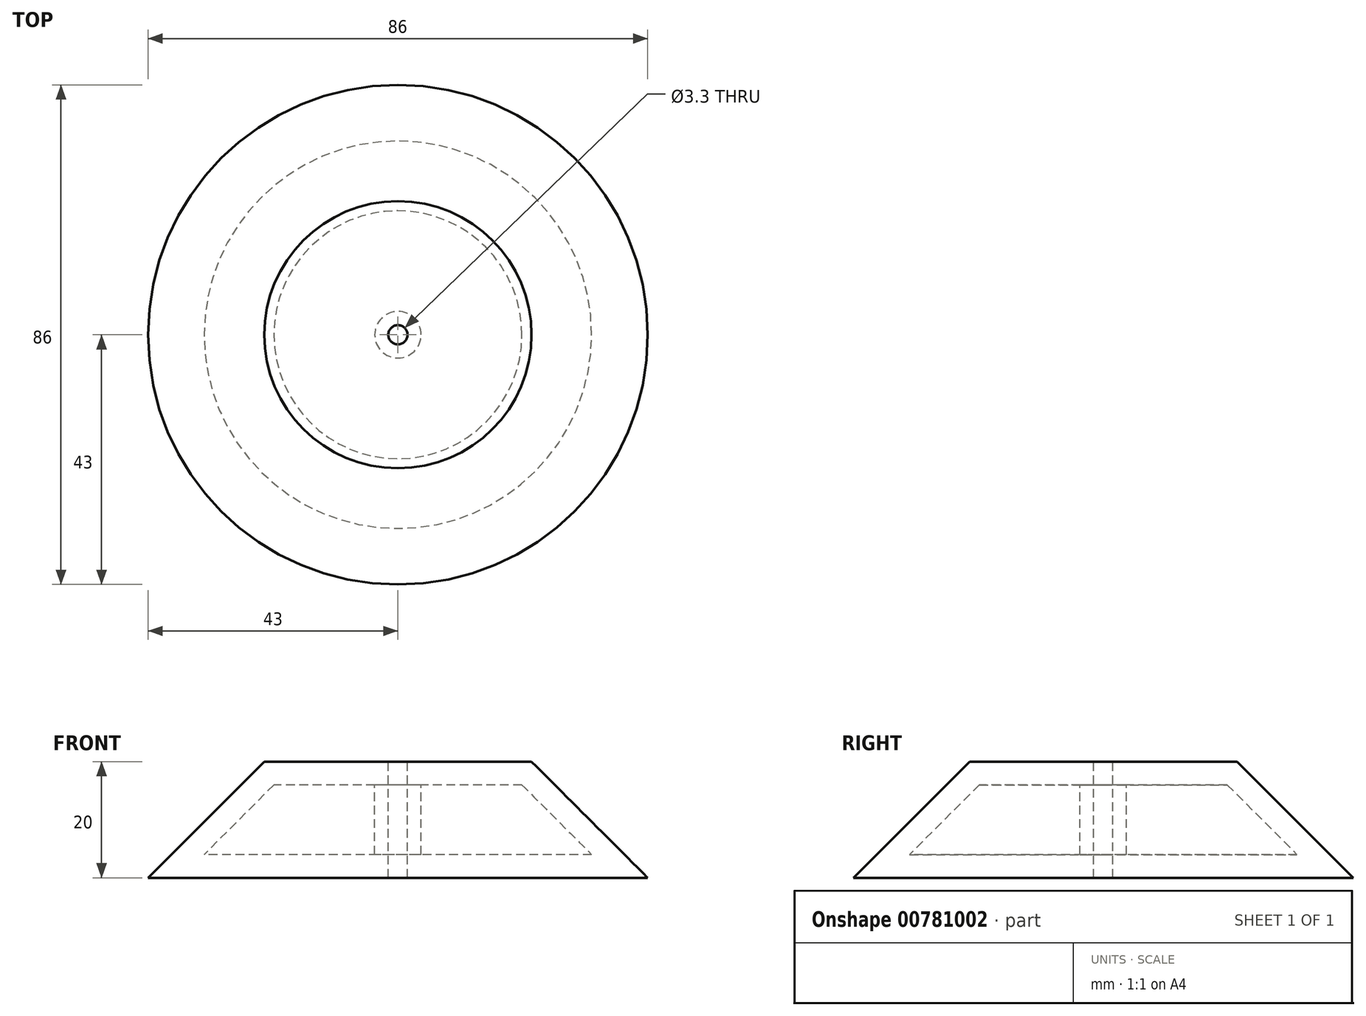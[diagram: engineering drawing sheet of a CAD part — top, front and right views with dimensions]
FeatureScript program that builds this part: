
annotation { "Feature Type Name" : "Feature", "Feature Type Description" : "" }
export const myFeature = defineFeature(function(context is Context, id is Id, definition is map)
    precondition{}
    {
        {
            var Q0;
            Q0=qCreatedBy(makeId("Front.planeOp"),FACE);
            var sketch = newSketch(context, id + "F0", { "sketchPlane" : qUnion([Q0])});
            skLineSegment(sketch, "E0.bottom", {"start": v(-23, 10) * mm, "end": v(0, 10) * mm});
            skLineSegment(sketch, "E0.top", {"start": v(-43, -10) * mm, "end": v(0, -10) * mm});
            skLineSegment(sketch, "E0.left", {"start": v(-23, 10) * mm, "end": v(-43, -10) * mm});
            skLineSegment(sketch, "E0.right", {"start": v(0, 10) * mm, "end": v(0, -10) * mm});
            skLineSegment(sketch, "E1.0", {"start": v(-21.34, 6) * mm, "end": v(-4, 6) * mm});
            skLineSegment(sketch, "E1.1", {"start": v(-21.34, 6) * mm, "end": v(-33.34, -6) * mm});
            skLineSegment(sketch, "E1.2", {"start": v(-33.34, -6) * mm, "end": v(-4, -6) * mm});
            skLineSegment(sketch, "E1.3", {"start": v(-4, 6) * mm, "end": v(-4, -6) * mm});
            skSolve(sketch);
        }
        {
            var Q0;
            Q0=makeQuery(id+"F0.imprint","IMPRINT",FACE,{"disambiguationData":[TD([[makeQuery(id+"F0.imprint","IMPRINT",EDGE,{"derivedFrom":sQuery(id+"F0.wireOp",EDGE,"E0.bottom")}),-1.0]])]});
            var Q1;
            Q1=sQuery(id+"F0.wireOp",EDGE,"E0.left");
            var Q2;
            Q2=sQuery(id+"F0.wireOp",EDGE,"E1.1");
            var Q3;
            Q3=sQuery(id+"F0.wireOp",EDGE,"E0.right");
            revolve(context, id + "F1", {"surfaceOperationType" : NewSurfaceOperationType.NEW, "entities" : qUnion([Q0]), "surfaceEntities" : qUnion([Q1, Q2]), "axis" : qUnion([Q3]), "revolveType" : RevolveType.FULL});
        }
        {
            var Q0;
            Q0=makeQuery(id+"F1.opRevolve","SWEPT_FACE",FACE,{"disambiguationData":[OSD([sQuery(id+"F0.wireOp",EDGE,"E0.bottom")])]});
            var sketch = newSketch(context, id + "F2", { "sketchPlane" : qUnion([Q0])});
            skCircle(sketch, "E2", {"center": v(0, 0) * mm, "radius": 2 * mm});
            skSolve(sketch);
        }
        {
            var Q0;
            Q0=sQuery(id+"F2.wireOp",VERTEX,"E2.center");
            var Q1;
            Q1=makeQuery(id+"F1.opRevolve","SWEPT_BODY",BODY,{"disambiguationData":[OSD([sQuery(id+"F0.wireOp",EDGE,"E0.bottom"),sQuery(id+"F0.wireOp",EDGE,"E0.top"),sQuery(id+"F0.wireOp",EDGE,"E0.left"),sQuery(id+"F0.wireOp",EDGE,"E0.right"),sQuery(id+"F0.wireOp",EDGE,"E1.0"),sQuery(id+"F0.wireOp",EDGE,"E1.1"),sQuery(id+"F0.wireOp",EDGE,"E1.2"),sQuery(id+"F0.wireOp",EDGE,"E1.3")])]});
            hole(context, id + "F3", {"style" : HoleStyle.SIMPLE, "endStyle" : HoleEndStyle.THROUGH, "standardTappedOrClearance" : lookupTablePath({ "standard" : "ISO", "engagement" : "75%", "pitch" : "0.7 mm", "size" : "M4", "type" : "Tapped" }), "standardBlindInLast" : lookupTablePath({ "standard" : "ISO", "engagement" : "75%", "pitch" : "0.7 mm", "size" : "M4", "type" : "Tapped" }), "holeDiameter" : 3.3 * mm, "majorDiameter" : 4 * mm, "showTappedDepth" : true, "isTappedThrough" : true, "tappedDepth" : 12 * mm, "tapClearance" : 3, "locations" : qUnion([Q0]), "scope" : qUnion([Q1])});
        }
    });
